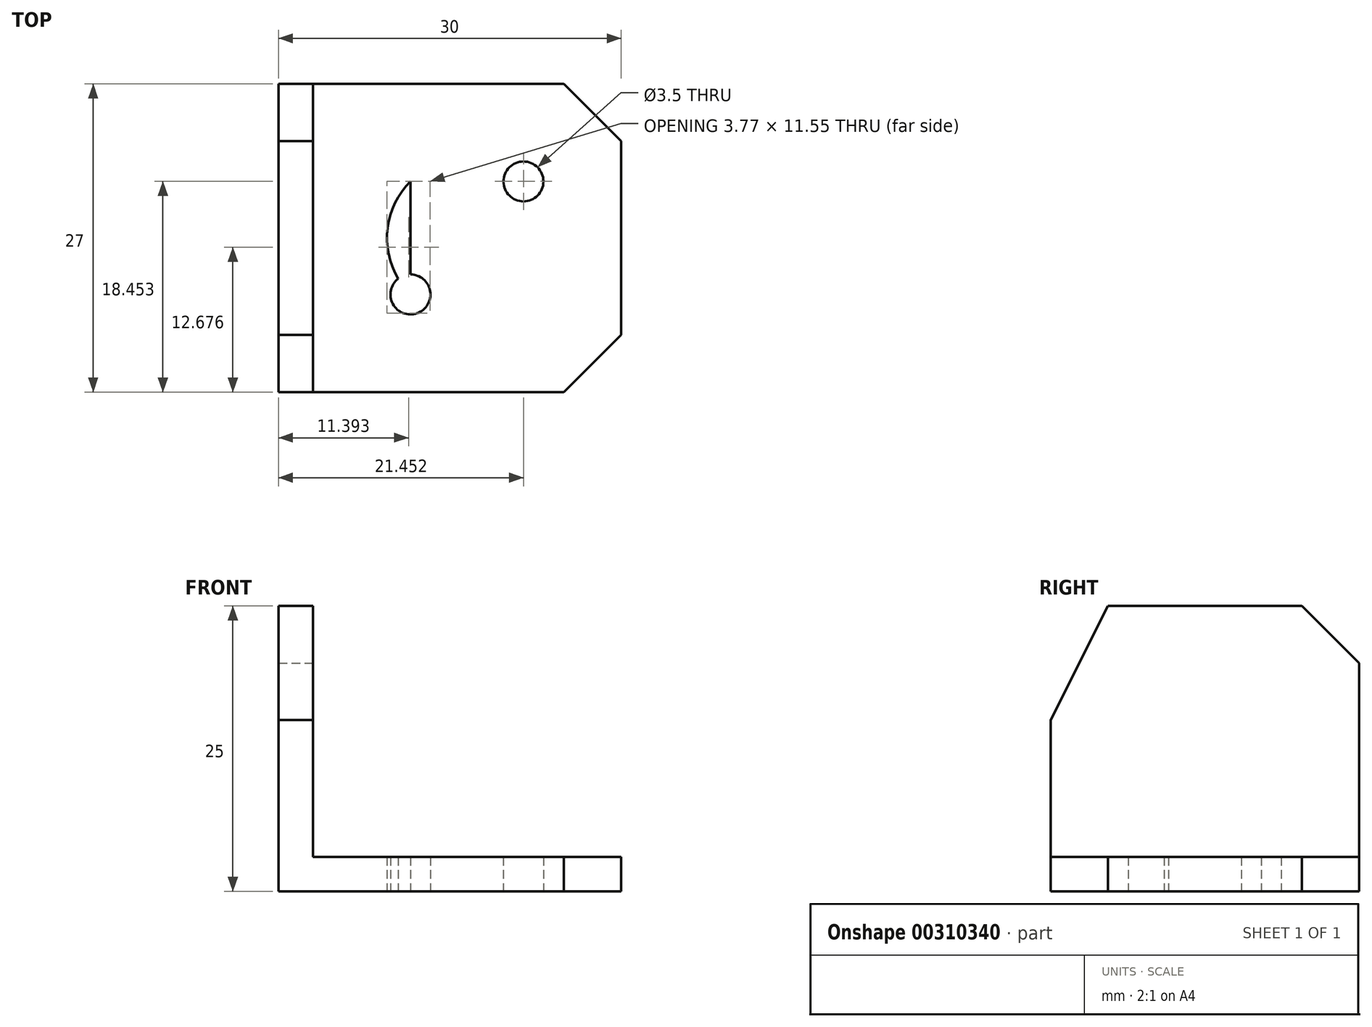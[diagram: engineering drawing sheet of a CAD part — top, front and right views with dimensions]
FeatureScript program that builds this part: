
annotation { "Feature Type Name" : "Feature", "Feature Type Description" : "" }
export const myFeature = defineFeature(function(context is Context, id is Id, definition is map)
    precondition{}
    {
        {
            var Q0;
            Q0=qCreatedBy(makeId("Top.planeOp"),FACE);
            var sketch = newSketch(context, id + "F0", { "sketchPlane" : qUnion([Q0])});
            skLineSegment(sketch, "E0.bottom", {"start": v(-4.6, 6.61) * mm, "end": v(25.4, 6.61) * mm});
            skLineSegment(sketch, "E0.top", {"start": v(-4.6, -20.39) * mm, "end": v(25.4, -20.39) * mm});
            skLineSegment(sketch, "E0.left", {"start": v(-1.6, 6.61) * mm, "end": v(-1.6, -20.39) * mm});
            skLineSegment(sketch, "E0.right", {"start": v(25.4, 6.61) * mm, "end": v(25.4, -20.39) * mm});
            skLineSegment(sketch, "E1.0", {"start": v(-4.6, 6.61) * mm, "end": v(-4.6, -20.39) * mm});
            skLineSegment(sketch, "E2.0", {"start": v(-4.6, -6.89) * mm, "end": v(25.4, -6.89) * mm});
            skPoint(sketch, "E3", {"position": v(11.9, -6.89) * mm});
            skCircle(sketch, "E4", {"center": v(11.9, -6.89) * mm, "radius": 7 * mm});
            skLineSegment(sketch, "E5.bottom", {"start": v(16.85, -1.94) * mm, "end": v(6.95, -1.94) * mm});
            skLineSegment(sketch, "E5.top", {"start": v(16.85, -11.84) * mm, "end": v(6.95, -11.84) * mm});
            skLineSegment(sketch, "E5.left", {"start": v(16.85, -1.94) * mm, "end": v(16.85, -11.84) * mm});
            skLineSegment(sketch, "E5.right", {"start": v(6.95, -1.94) * mm, "end": v(6.95, -11.84) * mm});
            skPoint(sketch, "E6", {"position": v(6.95, -1.94) * mm});
            skPoint(sketch, "E7", {"position": v(16.85, -1.94) * mm});
            skPoint(sketch, "E8", {"position": v(16.85, -11.84) * mm});
            skPoint(sketch, "E9", {"position": v(6.95, -11.84) * mm});
            skSolve(sketch);
        }
        {
            var Q0;
            {var subQ2=sQuery(id+"F0.wireOp",EDGE,"E0.left");Q0=makeQuery(id+"F0.imprint","IMPRINT",FACE,{"disambiguationData":[TD([[makeQuery(id+"F0.imprint","IMPRINT",EDGE,{"derivedFrom":subQ2}),1.0]])]});}
            var Q1;
            {var subQ0=sQuery(id+"F0.wireOp",EDGE,"d44c9173-2214-4bb4-829c-949c7a6de1a7.0");var subQ1=sQuery(id+"F0.wireOp",EDGE,"6d2577c0-8f8b-446b-954c-d693c8628348.0");var subQ2=makeQuery(id+"F0.imprint","INTERSECT",VERTEX,{"derivedFrom":[subQ1,subQ0]});Q1=makeQuery(id+"F0.imprint","IMPRINT",FACE,{"disambiguationData":[TD([[makeQuery(id+"F0.imprint","IMPRINT",EDGE,{"disambiguationData":[TD([[subQ2,-1.0]])],"derivedFrom":subQ1}),1.0]])]});}
            var Q2;
            {var subQ0=sQuery(id+"F0.wireOp",EDGE,"5cfc5a33-7ed8-4f07-9732-90347c7967e2.0");var subQ1=sQuery(id+"F0.wireOp",EDGE,"E0.top");var subQ2=makeQuery(id+"F0.imprint","INTERSECT",VERTEX,{"derivedFrom":[subQ1,subQ0]});Q2=makeQuery(id+"F0.imprint","IMPRINT",FACE,{"disambiguationData":[TD([[makeQuery(id+"F0.imprint","IMPRINT",EDGE,{"disambiguationData":[TD([[subQ2,1.0]])],"derivedFrom":subQ1}),1.0]])]});}
            var Q3;
            {var subQ0=sQuery(id+"F0.wireOp",EDGE,"5cfc5a33-7ed8-4f07-9732-90347c7967e2.0");var subQ1=sQuery(id+"F0.wireOp",EDGE,"E0.bottom");var subQ2=makeQuery(id+"F0.imprint","INTERSECT",VERTEX,{"derivedFrom":[subQ1,subQ0]});Q3=makeQuery(id+"F0.imprint","IMPRINT",FACE,{"disambiguationData":[TD([[makeQuery(id+"F0.imprint","IMPRINT",EDGE,{"disambiguationData":[TD([[subQ2,1.0]])],"derivedFrom":subQ1}),-1.0]])]});}
            var Q4;
            {var subQ0=sQuery(id+"F0.wireOp",EDGE,"E0.right");var subQ1=sQuery(id+"F0.wireOp",EDGE,"E0.bottom");var subQ2=makeQuery(id+"F0.imprint","INTERSECT",VERTEX,{"derivedFrom":[subQ1,subQ0]});Q4=makeQuery(id+"F0.imprint","IMPRINT",FACE,{"disambiguationData":[TD([[makeQuery(id+"F0.imprint","IMPRINT",EDGE,{"disambiguationData":[TD([[subQ2,1.0]])],"derivedFrom":subQ1}),-1.0]])]});}
            var Q5;
            {var subQ0=sQuery(id+"F0.wireOp",EDGE,"E0.right");var subQ1=sQuery(id+"F0.wireOp",EDGE,"E0.top");var subQ2=makeQuery(id+"F0.imprint","INTERSECT",VERTEX,{"derivedFrom":[subQ1,subQ0]});Q5=makeQuery(id+"F0.imprint","IMPRINT",FACE,{"disambiguationData":[TD([[makeQuery(id+"F0.imprint","IMPRINT",EDGE,{"disambiguationData":[TD([[subQ2,1.0]])],"derivedFrom":subQ1}),1.0]])]});}
            var Q6;
            {var subQ0=sQuery(id+"F0.wireOp",EDGE,"6d2577c0-8f8b-446b-954c-d693c8628348.0");var subQ1=sQuery(id+"F0.wireOp",EDGE,"E0.right");var subQ2=makeQuery(id+"F0.imprint","INTERSECT",VERTEX,{"derivedFrom":[subQ1,subQ0]});Q6=makeQuery(id+"F0.imprint","IMPRINT",FACE,{"disambiguationData":[TD([[makeQuery(id+"F0.imprint","IMPRINT",EDGE,{"disambiguationData":[TD([[subQ2,1.0]])],"derivedFrom":subQ1}),-1.0]])]});}
            var Q7;
            {var subQ0=sQuery(id+"F0.wireOp",EDGE,"E5.bottom");Q7=makeQuery(id+"F0.imprint","IMPRINT",FACE,{"disambiguationData":[TD([[makeQuery(id+"F0.imprint","IMPRINT",EDGE,{"derivedFrom":subQ0}),-1.0]])]});}
            var Q8;
            {var subQ0=sQuery(id+"F0.wireOp",EDGE,"E4");var subQ1=sQuery(id+"F0.wireOp",EDGE,"E2.0");var subQ2=makeQuery(id+"F0.imprint","INTERSECT",VERTEX,{"disambiguationData":[OD(0.0)],"derivedFrom":[subQ1,subQ0]});Q8=makeQuery(id+"F0.imprint","IMPRINT",FACE,{"disambiguationData":[TD([[makeQuery(id+"F0.imprint","IMPRINT",EDGE,{"disambiguationData":[TD([[subQ2,-1.0]])],"derivedFrom":subQ1}),1.0]])]});}
            var Q9;
            {var subQ5=sQuery(id+"F0.wireOp",EDGE,"E5.bottom");Q9=makeQuery(id+"F0.imprint","IMPRINT",FACE,{"disambiguationData":[TD([[makeQuery(id+"F0.imprint","IMPRINT",EDGE,{"derivedFrom":subQ5}),1.0]])]});}
            var Q10;
            {var subQ0=sQuery(id+"F0.wireOp",EDGE,"E5.left");var subQ1=sQuery(id+"F0.wireOp",EDGE,"E2.0");var subQ2=makeQuery(id+"F0.imprint","INTERSECT",VERTEX,{"derivedFrom":[subQ1,subQ0]});Q10=makeQuery(id+"F0.imprint","IMPRINT",FACE,{"disambiguationData":[TD([[makeQuery(id+"F0.imprint","IMPRINT",EDGE,{"disambiguationData":[TD([[subQ2,-1.0]])],"derivedFrom":subQ1}),1.0]])]});}
            var Q11;
            {var subQ0=sQuery(id+"F0.wireOp",EDGE,"E5.left");var subQ1=sQuery(id+"F0.wireOp",EDGE,"E2.0");var subQ2=makeQuery(id+"F0.imprint","INTERSECT",VERTEX,{"derivedFrom":[subQ1,subQ0]});Q11=makeQuery(id+"F0.imprint","IMPRINT",FACE,{"disambiguationData":[TD([[makeQuery(id+"F0.imprint","IMPRINT",EDGE,{"disambiguationData":[TD([[subQ2,-1.0]])],"derivedFrom":subQ1}),-1.0]])]});}
            var Q12;
            {var subQ5=sQuery(id+"F0.wireOp",EDGE,"E5.top");Q12=makeQuery(id+"F0.imprint","IMPRINT",FACE,{"disambiguationData":[TD([[makeQuery(id+"F0.imprint","IMPRINT",EDGE,{"derivedFrom":subQ5}),-1.0]])]});}
            var Q13;
            {var subQ0=sQuery(id+"F0.wireOp",EDGE,"E4");var subQ1=sQuery(id+"F0.wireOp",EDGE,"E2.0");var subQ2=makeQuery(id+"F0.imprint","INTERSECT",VERTEX,{"disambiguationData":[OD(0.0)],"derivedFrom":[subQ1,subQ0]});Q13=makeQuery(id+"F0.imprint","IMPRINT",FACE,{"disambiguationData":[TD([[makeQuery(id+"F0.imprint","IMPRINT",EDGE,{"disambiguationData":[TD([[subQ2,-1.0]])],"derivedFrom":subQ1}),-1.0]])]});}
            var Q14;
            {var subQ0=sQuery(id+"F0.wireOp",EDGE,"E5.top");Q14=makeQuery(id+"F0.imprint","IMPRINT",FACE,{"disambiguationData":[TD([[makeQuery(id+"F0.imprint","IMPRINT",EDGE,{"derivedFrom":subQ0}),1.0]])]});}
            extrude(context, id + "F1", {"entities" : qUnion([Q0, Q1, Q2, Q3, Q4, Q5, Q6, Q7, Q8, Q9, Q10, Q11, Q12, Q13, Q14]), "depth" : 3 * mm});
        }
        {
            var Q0;
            {var subQ2=sQuery(id+"F0.wireOp",EDGE,"E0.left");Q0=makeQuery(id+"F0.imprint","IMPRINT",FACE,{"disambiguationData":[TD([[makeQuery(id+"F0.imprint","IMPRINT",EDGE,{"derivedFrom":subQ2}),-1.0]])]});}
            extrude(context, id + "F2", {"entities" : qUnion([Q0]), "operationType" : NewBodyOperationType.ADD, "depth" : 25 * mm});
        }
        {
            var Q0;
            Q0=sQuery(id+"F0.wireOp",VERTEX,"E7");
            var Q1;
            Q1=sQuery(id+"F0.wireOp",VERTEX,"E9");
            var Q2;
            Q2=makeQuery(id+"F1.opExtrude","SWEPT_BODY",BODY,{"disambiguationData":[OSD([sQuery(id+"F0.wireOp",EDGE,"E0.bottom"),sQuery(id+"F0.wireOp",EDGE,"E0.top"),sQuery(id+"F0.wireOp",EDGE,"E0.left"),sQuery(id+"F0.wireOp",EDGE,"E0.right")])]});
            hole(context, id + "F3", {"style" : HoleStyle.SIMPLE, "endStyle" : HoleEndStyle.BLIND, "oppositeDirection" : true, "holeDiameter" : 3.5 * mm, "holeDepth" : 12.4 * mm, "tappedDepth" : 10 * mm, "tapClearance" : 3, "startFromSketch" : true, "locations" : qUnion([Q0, Q1]), "scope" : qUnion([Q2])});
        }
        {
            var Q0;
            {var subQ0=sQuery(id+"F0.wireOp",EDGE,"E1.0");Q0=makeQuery(id+"F2.boolean.opBoolean","MERGE",FACE,{"derivedFrom":[makeQuery(id+"F1.opExtrude","SWEPT_FACE",FACE,{"disambiguationData":[OSD([subQ0])]}),makeQuery(id+"F2.opExtrude","SWEPT_FACE",FACE,{"disambiguationData":[OSD([subQ0])]})]});}
            var sketch = newSketch(context, id + "F4", { "sketchPlane" : qUnion([Q0])});
            skLineSegment(sketch, "E10.bottom", {"start": v(-6.61, 25) * mm, "end": v(20.39, 25) * mm});
            skLineSegment(sketch, "E10.top", {"start": v(-6.61, 0) * mm, "end": v(20.39, 0) * mm});
            skLineSegment(sketch, "E10.left", {"start": v(-6.61, 25) * mm, "end": v(-6.61, 0) * mm});
            skLineSegment(sketch, "E10.right", {"start": v(20.39, 25) * mm, "end": v(20.39, 0) * mm});
            skLineSegment(sketch, "E11.0", {"start": v(15.39, 25) * mm, "end": v(15.39, 0) * mm});
            skLineSegment(sketch, "E12.0", {"start": v(-6.61, 15) * mm, "end": v(20.39, 15) * mm});
            skLineSegment(sketch, "E13", {"start": v(15.39, 25) * mm, "end": v(20.39, 15) * mm});
            skSolve(sketch);
        }
        {
            var Q0;
            {var subQ3=sQuery(id+"F4.wireOp",EDGE,"E13");Q0=makeQuery(id+"F4.imprint","IMPRINT",FACE,{"disambiguationData":[TD([[makeQuery(id+"F4.imprint","IMPRINT",EDGE,{"derivedFrom":subQ3}),1.0]])]});}
            extrude(context, id + "F5", {"entities" : qUnion([Q0]), "operationType" : NewBodyOperationType.REMOVE, "endBound" : BoundingType.THROUGH_ALL, "oppositeDirection" : true, "depth" : 25 * mm});
        }
        {
            var Q0;
            Q0=makeQuery(id+"F1.opExtrude","SWEPT_EDGE",EDGE,{"disambiguationData":[OSD([sQuery(id+"F0.wireOp",EDGE,"E0.top"),sQuery(id+"F0.wireOp",EDGE,"E0.right")])]});
            var Q1;
            Q1=makeQuery(id+"F1.opExtrude","SWEPT_EDGE",EDGE,{"disambiguationData":[OSD([sQuery(id+"F0.wireOp",EDGE,"E0.bottom"),sQuery(id+"F0.wireOp",EDGE,"E0.right")])]});
            var Q2;
            Q2=makeQuery(id+"F2.opExtrude","CAP_EDGE",EDGE,{"disambiguationData":[OSD([sQuery(id+"F0.wireOp",EDGE,"E0.bottom")])],"isStart":false});
            chamfer(context, id + "F6", {"entities" : qUnion([Q0, Q1, Q2]), "width" : 5 * mm, "tangentPropagation" : true});
        }
    });
